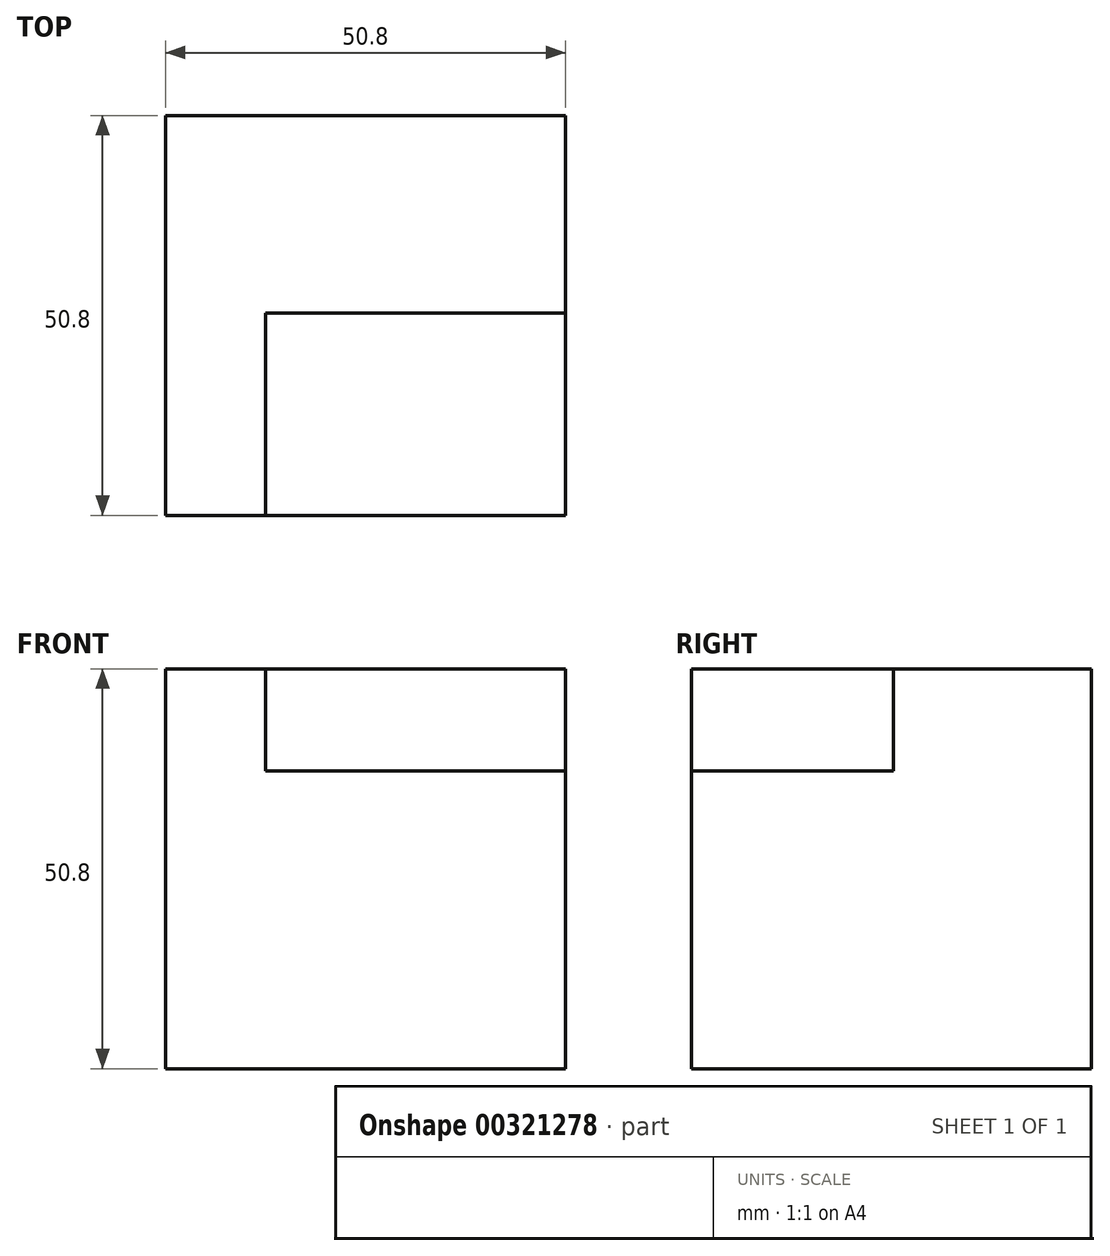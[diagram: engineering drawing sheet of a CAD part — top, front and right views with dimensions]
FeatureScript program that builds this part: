
annotation { "Feature Type Name" : "Feature", "Feature Type Description" : "" }
export const myFeature = defineFeature(function(context is Context, id is Id, definition is map)
    precondition{}
    {
        {
            var Q0;
            Q0=qCreatedBy(makeId("Front.planeOp"),FACE);
            var sketch = newSketch(context, id + "F0", { "sketchPlane" : qUnion([Q0])});
            skLineSegment(sketch, "E0", {"start": v(6.87, -18.4) * mm, "end": v(-43.93, -18.4) * mm});
            skLineSegment(sketch, "E1", {"start": v(6.87, -18.4) * mm, "end": v(6.87, 32.4) * mm});
            skLineSegment(sketch, "E2", {"start": v(-43.93, -18.4) * mm, "end": v(-43.93, 32.4) * mm});
            skLineSegment(sketch, "E3", {"start": v(-43.93, 32.4) * mm, "end": v(6.87, 32.4) * mm});
            skSolve(sketch);
        }
        {
            var Q0;
            Q0=makeQuery(id+"F0.imprint","IMPRINT",FACE,{"disambiguationData":[TD([[makeQuery(id+"F0.imprint","IMPRINT",EDGE,{"derivedFrom":sQuery(id+"F0.wireOp",EDGE,"E0")}),-1.0]])]});
            extrude(context, id + "F1", {"entities" : qUnion([Q0]), "depth" : 50.8 * mm});
        }
        {
            var Q0;
            Q0=makeQuery(id+"F1.opExtrude","CAP_FACE",FACE,{"disambiguationData":[OSD([sQuery(id+"F0.wireOp",EDGE,"E0"),sQuery(id+"F0.wireOp",EDGE,"E1"),sQuery(id+"F0.wireOp",EDGE,"E2"),sQuery(id+"F0.wireOp",EDGE,"E3")])],"isStart":false});
            var sketch = newSketch(context, id + "F2", { "sketchPlane" : qUnion([Q0])});
            skLineSegment(sketch, "E4.bottom", {"start": v(0, 17.5) * mm, "end": v(25.4, 17.5) * mm});
            skLineSegment(sketch, "E4.top", {"start": v(0, 42.9) * mm, "end": v(25.4, 42.9) * mm});
            skLineSegment(sketch, "E4.left", {"start": v(0, 17.5) * mm, "end": v(0, 42.9) * mm});
            skLineSegment(sketch, "E4.right", {"start": v(25.4, 17.5) * mm, "end": v(25.4, 42.9) * mm});
            skSolve(sketch);
        }
        {
            var Q0;
            {var subQ2=sQuery(id+"F2.wireOp",EDGE,"E4.top");Q0=makeQuery(id+"F2.imprint","IMPRINT",FACE,{"disambiguationData":[TD([[makeQuery(id+"F2.imprint","IMPRINT",EDGE,{"derivedFrom":subQ2}),-1.0]])]});}
            extrude(context, id + "F3", {"entities" : qUnion([Q0]), "operationType" : NewBodyOperationType.REMOVE, "oppositeDirection" : true, "depth" : 38.1 * mm});
        }
        {
            var Q0;
            Q0=makeQuery(id+"F1.opExtrude","SWEPT_FACE",FACE,{"disambiguationData":[OSD([sQuery(id+"F0.wireOp",EDGE,"E1")])]});
            var sketch = newSketch(context, id + "F4", { "sketchPlane" : qUnion([Q0])});
            skLineSegment(sketch, "E5.bottom", {"start": v(-63.23, 19.42) * mm, "end": v(-37.83, 19.42) * mm});
            skLineSegment(sketch, "E5.top", {"start": v(-63.23, 44.82) * mm, "end": v(-37.83, 44.82) * mm});
            skLineSegment(sketch, "E5.left", {"start": v(-63.23, 19.42) * mm, "end": v(-63.23, 44.82) * mm});
            skLineSegment(sketch, "E5.right", {"start": v(-37.83, 19.42) * mm, "end": v(-37.83, 44.82) * mm});
            skSolve(sketch);
        }
        {
            var Q0;
            {var subQ0=sQuery(id+"F4.wireOp",EDGE,"E5.right");var subQ1=sQuery(id+"F4.wireOp",EDGE,"E5.bottom");var subQ2=makeQuery(id+"F4.imprint","INTERSECT",VERTEX,{"derivedFrom":[subQ1,subQ0]});Q0=makeQuery(id+"F4.imprint","IMPRINT",FACE,{"disambiguationData":[TD([[makeQuery(id+"F4.imprint","IMPRINT",EDGE,{"disambiguationData":[TD([[subQ2,1.0]])],"derivedFrom":subQ1}),1.0]])]});}
            extrude(context, id + "F5", {"entities" : qUnion([Q0]), "operationType" : NewBodyOperationType.REMOVE, "oppositeDirection" : true, "depth" : 38.1 * mm});
        }
        {
            var Q0;
            Q0=makeQuery(id+"F5.boolean.opBoolean","COPY",FACE,{"derivedFrom":makeQuery(id+"F5.opExtrude","SWEPT_FACE",FACE,{"disambiguationData":[OSD([sQuery(id+"F4.wireOp",EDGE,"E5.right")])]})});
            extrude(context, id + "F6", {"entities" : qUnion([Q0]), "operationType" : NewBodyOperationType.ADD, "oppositeDirection" : true, "depth" : 12.7 * mm});
        }
        {
            var Q0;
            Q0=makeQuery(id+"F5.boolean.opBoolean","COPY",FACE,{"derivedFrom":makeQuery(id+"F5.opExtrude","SWEPT_FACE",FACE,{"disambiguationData":[OSD([sQuery(id+"F4.wireOp",EDGE,"E5.right")])]})});
            extrude(context, id + "F7", {"entities" : qUnion([Q0]), "operationType" : NewBodyOperationType.REMOVE, "oppositeDirection" : true, "depth" : 12.7 * mm});
        }
    });
